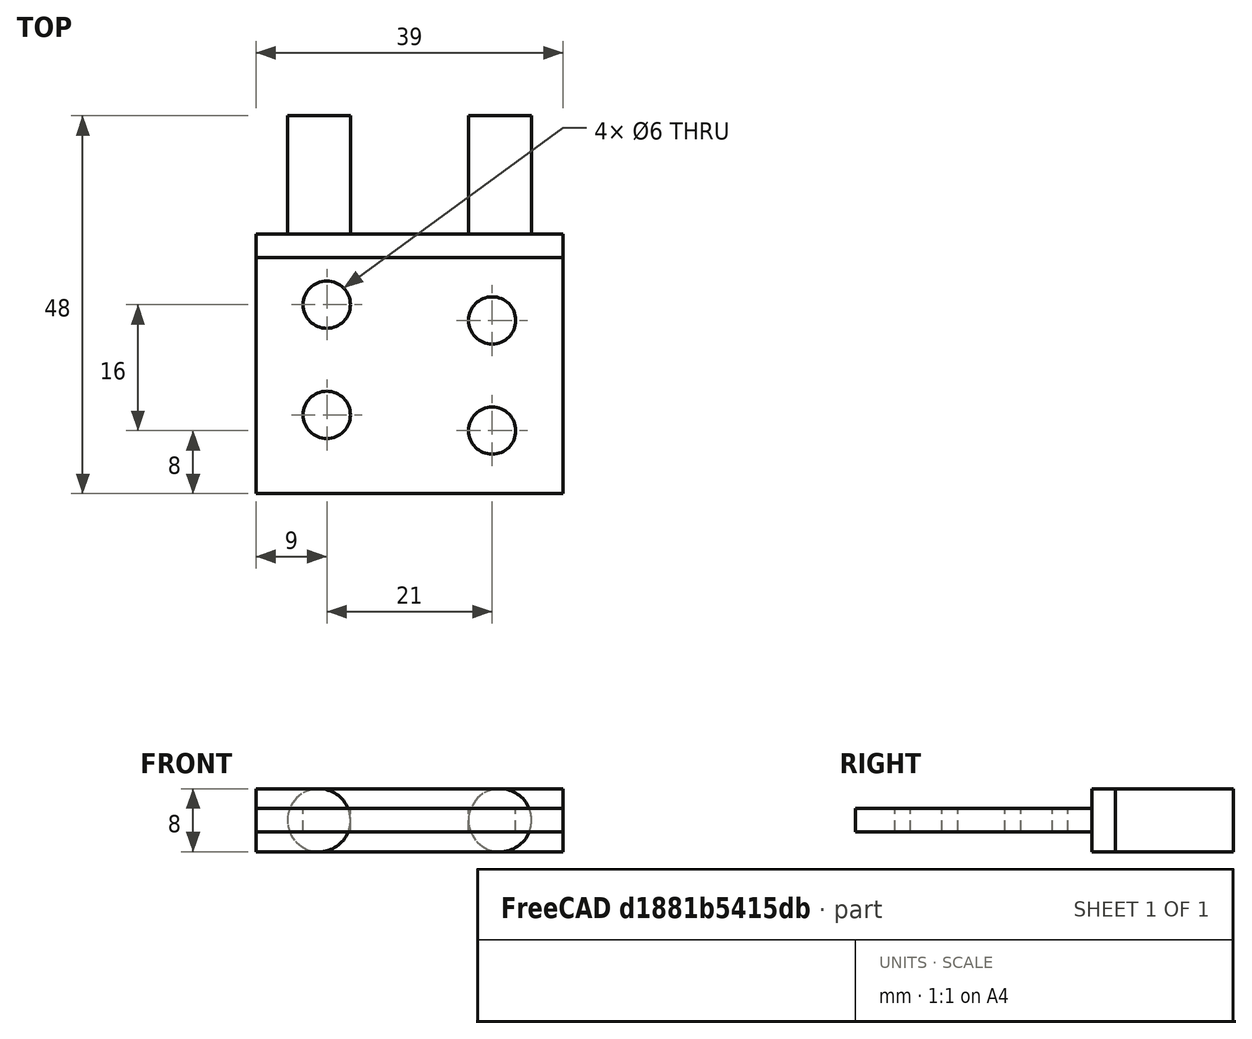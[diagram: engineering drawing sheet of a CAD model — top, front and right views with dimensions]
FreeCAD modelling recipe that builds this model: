
FCSTD DOCUMENT  (FreeCAD 0.15R4671 (Git))
Label: Holder_V2
License: All rights reserved
LicenseURL: http://en.wikipedia.org/wiki/All_rights_reserved
objects: Part::Cylinder×6, Part::Box×2, Part::MultiFuse×1, Part::Cut×1
note: 10 computed .brp shape members not serialized (recipe doc carries the construction recipe); baked Part::Feature solids carry a one-line shape summary decoded from their .brp

FEATURE [Part::Box] Box  label="Base"
  Height = 8
  Length = 39
  Placement = pos=(-8,-18,-4) rot=(0,0,1;0rad)
  Width = 3
FEATURE [Part::Cylinder] Cylinder  label="Pin2"
  Angle = 360
  Height = 15
  Placement = pos=(23,0,0) rot=(1,0,0;1.5708rad)
  Radius = 4
FEATURE [Part::Cylinder] Cylinder001  label="Pin1"
  Angle = 360
  Height = 15
  Placement = pos=(0,0,0) rot=(1,0,0;1.5708rad)
  Radius = 4
FEATURE [Part::Box] Box001  label="Holder"
  Height = 3
  Length = 39
  Placement = pos=(-8,-48,-1.5) rot=(0,0,1;0rad)
  Width = 30
FEATURE [Part::Cylinder] Cylinder002  label="Cut1"
  Angle = 360
  Height = 3
  Placement = pos=(22,-26,-1.5) rot=(0,0,1;0rad)
  Radius = 3
FEATURE [Part::Cylinder] Cylinder003  label="Cut2"
  Angle = 360
  Height = 3
  Placement = pos=(1,-24,-1.5) rot=(0,0,1;0rad)
  Radius = 3
FEATURE [Part::Cylinder] Cylinder004  label="Cut3"
  Angle = 360
  Height = 3
  Placement = pos=(1,-38,-1.5) rot=(0,0,1;0rad)
  Radius = 3
FEATURE [Part::Cylinder] Cylinder005  label="Cut4"
  Angle = 360
  Height = 3
  Placement = pos=(22,-40,-1.5) rot=(0,0,1;0rad)
  Radius = 3
FEATURE [Part::MultiFuse] Fusion
  Shapes = -> [Cylinder005,Cylinder004,Cylinder003,Cylinder002]
FEATURE [Part::Cut] Cut
  Base = -> Box001
  Tool = -> Fusion
